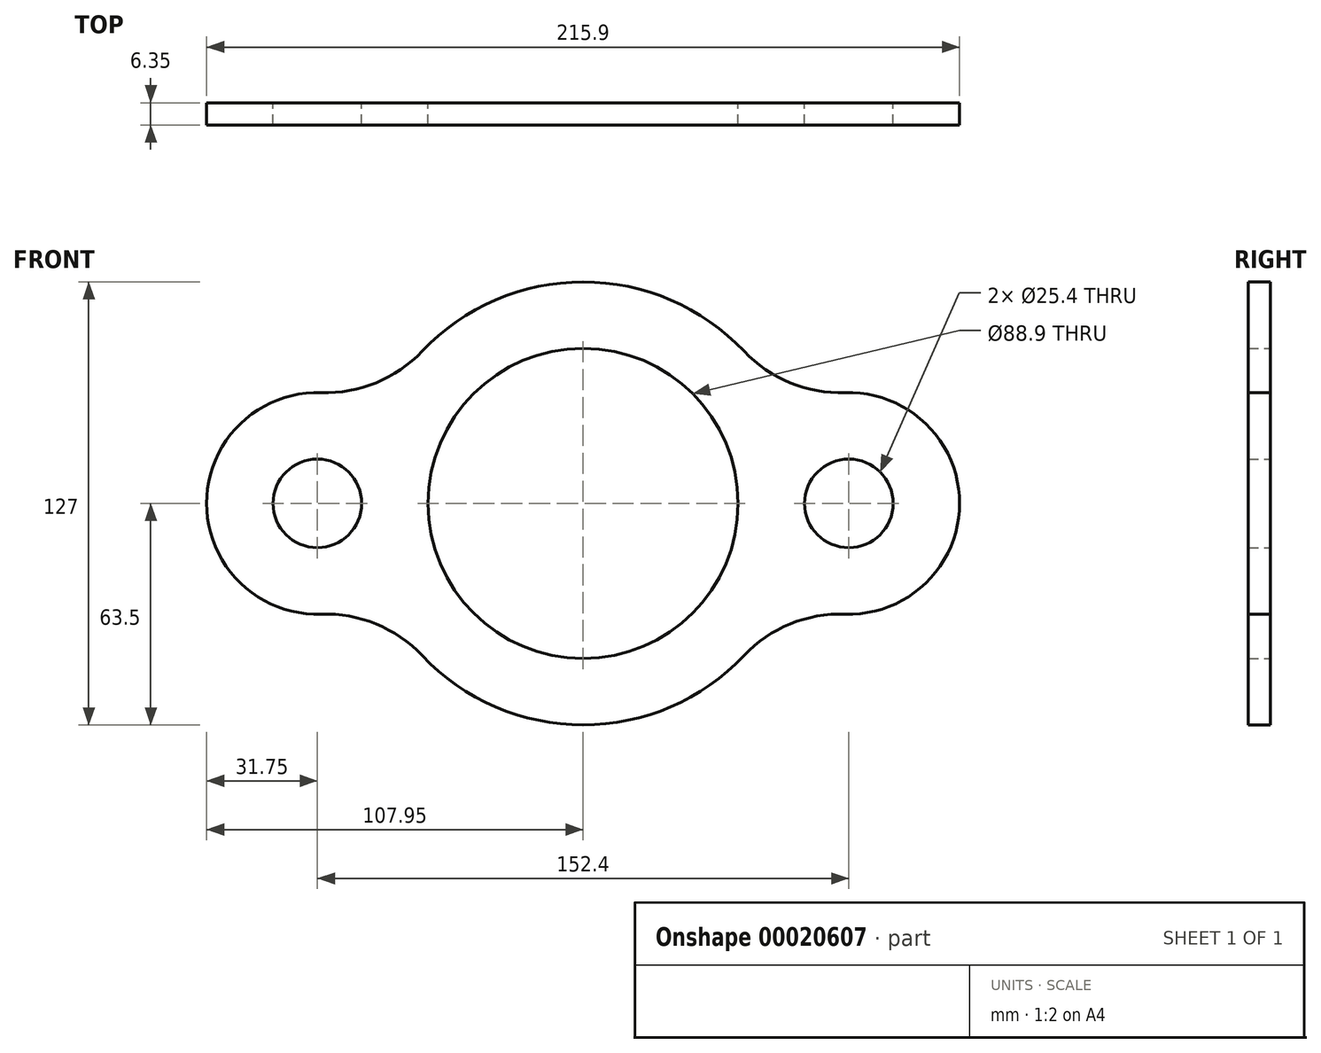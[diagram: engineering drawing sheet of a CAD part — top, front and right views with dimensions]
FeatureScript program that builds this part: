
annotation { "Feature Type Name" : "Feature", "Feature Type Description" : "" }
export const myFeature = defineFeature(function(context is Context, id is Id, definition is map)
    precondition{}
    {
        {
            var Q0;
            Q0=qCreatedBy(makeId("Front.planeOp"),FACE);
            var sketch = newSketch(context, id + "F0", { "sketchPlane" : qUnion([Q0])});
            skCircle(sketch, "E0", {"center": v(0, 0) * mm, "radius": 44.45 * mm});
            skArc(sketch, "E1", {"start": v(-46.14, -43.63) * mm, "mid": v(0, -63.5) * mm, "end": v(46.14, -43.63) * mm});
            skCircle(sketch, "E2", {"center": v(76.2, 0) * mm, "radius": 12.7 * mm});
            skArc(sketch, "E3", {"start": v(75.12, -31.73) * mm, "mid": v(107.95, 0) * mm, "end": v(75.12, 31.73) * mm});
            skCircle(sketch, "E4", {"center": v(-76.2, 0) * mm, "radius": 12.7 * mm});
            skArc(sketch, "E5", {"start": v(-75.12, 31.73) * mm, "mid": v(-107.95, 0) * mm, "end": v(-75.12, -31.73) * mm});
            skArc(sketch, "E6.trimOffspring", {"start": v(46.14, 43.63) * mm, "mid": v(0, 63.5) * mm, "end": v(-46.14, 43.63) * mm});
            skPoint(sketch, "E7.visualSharp", {"position": v(-57.94, 25.98) * mm});
            skArc(sketch, "E7.filletArc", {"start": v(-75.12, 31.73) * mm, "mid": v(-59.35, 34.56) * mm, "end": v(-46.14, 43.63) * mm});
            skPoint(sketch, "E8.visualSharp", {"position": v(-57.94, -25.98) * mm});
            skArc(sketch, "E8.filletArc", {"start": v(-46.14, -43.63) * mm, "mid": v(-59.35, -34.56) * mm, "end": v(-75.12, -31.73) * mm});
            skPoint(sketch, "E9.visualSharp", {"position": v(57.94, -25.98) * mm});
            skArc(sketch, "E9.filletArc", {"start": v(75.12, -31.73) * mm, "mid": v(59.35, -34.56) * mm, "end": v(46.14, -43.63) * mm});
            skPoint(sketch, "E10.visualSharp", {"position": v(57.94, 25.98) * mm});
            skArc(sketch, "E10.filletArc", {"start": v(46.14, 43.63) * mm, "mid": v(59.35, 34.56) * mm, "end": v(75.12, 31.73) * mm});
            skSolve(sketch);
        }
        {
            var Q0;
            Q0=makeQuery(id+"F0.imprint","IMPRINT",FACE,{"disambiguationData":[TD([[makeQuery(id+"F0.imprint","IMPRINT",EDGE,{"derivedFrom":sQuery(id+"F0.wireOp",EDGE,"E0")}),-1.0]])]});
            extrude(context, id + "F1", {"entities" : qUnion([Q0]), "depth" : 6.35 * mm});
        }
    });
